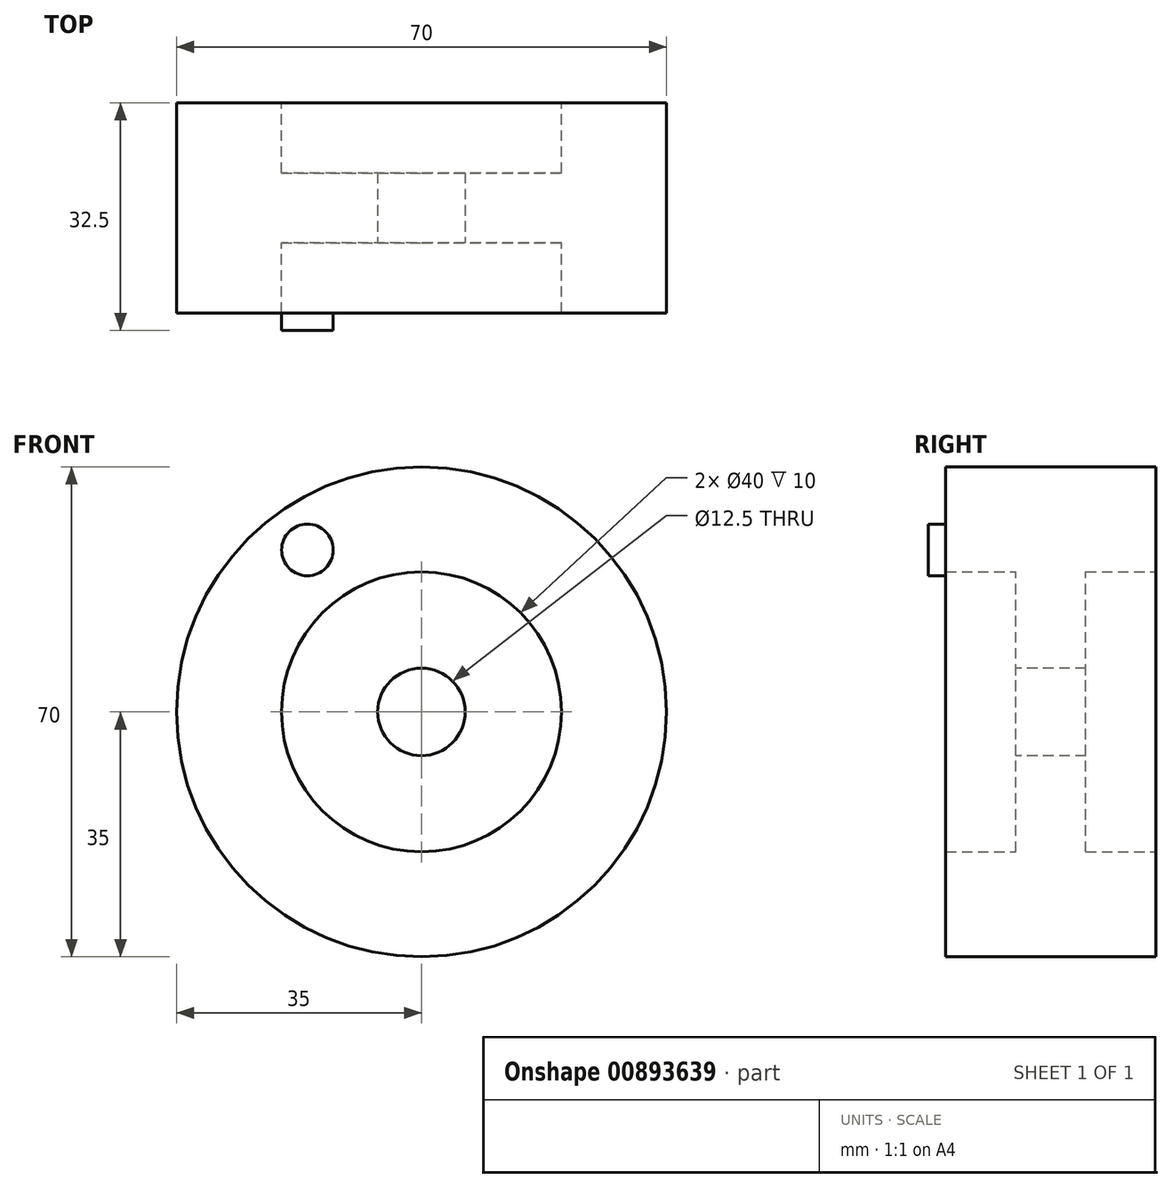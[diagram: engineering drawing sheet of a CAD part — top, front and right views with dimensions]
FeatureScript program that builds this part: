
annotation { "Feature Type Name" : "Feature", "Feature Type Description" : "" }
export const myFeature = defineFeature(function(context is Context, id is Id, definition is map)
    precondition{}
    {
        {
            var Q0;
            Q0=qCreatedBy(makeId("Front.planeOp"),FACE);
            var sketch = newSketch(context, id + "F0", { "sketchPlane" : qUnion([Q0])});
            skCircle(sketch, "E0", {"center": v(0, 0) * mm, "radius": 35 * mm});
            skCircle(sketch, "E1", {"center": v(0, 0) * mm, "radius": 20 * mm});
            skSolve(sketch);
        }
        {
            var Q0;
            Q0=makeQuery(id+"F0.imprint","IMPRINT",FACE,{"disambiguationData":[TD([[makeQuery(id+"F0.imprint","IMPRINT",EDGE,{"derivedFrom":sQuery(id+"F0.wireOp",EDGE,"E0")}),1.0]])]});
            extrude(context, id + "F1", {"entities" : qUnion([Q0]), "endBound" : BoundingType.SYMMETRIC, "depth" : 30 * mm, "offsetDistance" : 25 * mm});
        }
        {
            var Q0;
            Q0=makeQuery(id+"F0.imprint","IMPRINT",FACE,{"disambiguationData":[TD([[makeQuery(id+"F0.imprint","IMPRINT",EDGE,{"derivedFrom":sQuery(id+"F0.wireOp",EDGE,"E1")}),1.0]])]});
            extrude(context, id + "F2", {"entities" : qUnion([Q0]), "operationType" : NewBodyOperationType.ADD, "endBound" : BoundingType.SYMMETRIC, "depth" : 10 * mm, "offsetDistance" : 25 * mm});
        }
        {
            var Q0;
            Q0=makeQuery(id+"F2.opExtrude","CAP_FACE",FACE,{"disambiguationData":[OSD([sQuery(id+"F0.wireOp",EDGE,"E1")])],"isStart":false});
            var sketch = newSketch(context, id + "F3", { "sketchPlane" : qUnion([Q0])});
            skCircle(sketch, "E2", {"center": v(0, 0) * mm, "radius": 6.25 * mm});
            skSolve(sketch);
        }
        {
            var Q0;
            Q0=makeQuery(id+"F3.imprint","IMPRINT",FACE,{"disambiguationData":[TD([[makeQuery(id+"F3.imprint","IMPRINT",EDGE,{"derivedFrom":sQuery(id+"F3.wireOp",EDGE,"E2")}),1.0]])]});
            extrude(context, id + "F4", {"entities" : qUnion([Q0]), "operationType" : NewBodyOperationType.REMOVE, "endBound" : BoundingType.SYMMETRIC, "oppositeDirection" : true, "depth" : 40 * mm, "offsetDistance" : 25 * mm});
        }
        {
            var Q0;
            Q0=makeQuery(id+"F1.opExtrude","CAP_FACE",FACE,{"disambiguationData":[OSD([sQuery(id+"F0.wireOp",EDGE,"E0"),sQuery(id+"F0.wireOp",EDGE,"E1")])],"isStart":false});
            var sketch = newSketch(context, id + "F5", { "sketchPlane" : qUnion([Q0])});
            skCircle(sketch, "E3", {"center": v(-16.3, 23.14) * mm, "radius": 3.69 * mm});
            skSolve(sketch);
        }
        {
            var Q0;
            Q0 = qSketchRegion(id + "F5", true);
            extrude(context, id + "F6", {"entities" : qUnion([Q0]), "operationType" : NewBodyOperationType.ADD, "depth" : 2.5 * mm, "offsetDistance" : 25 * mm});
        }
    });
